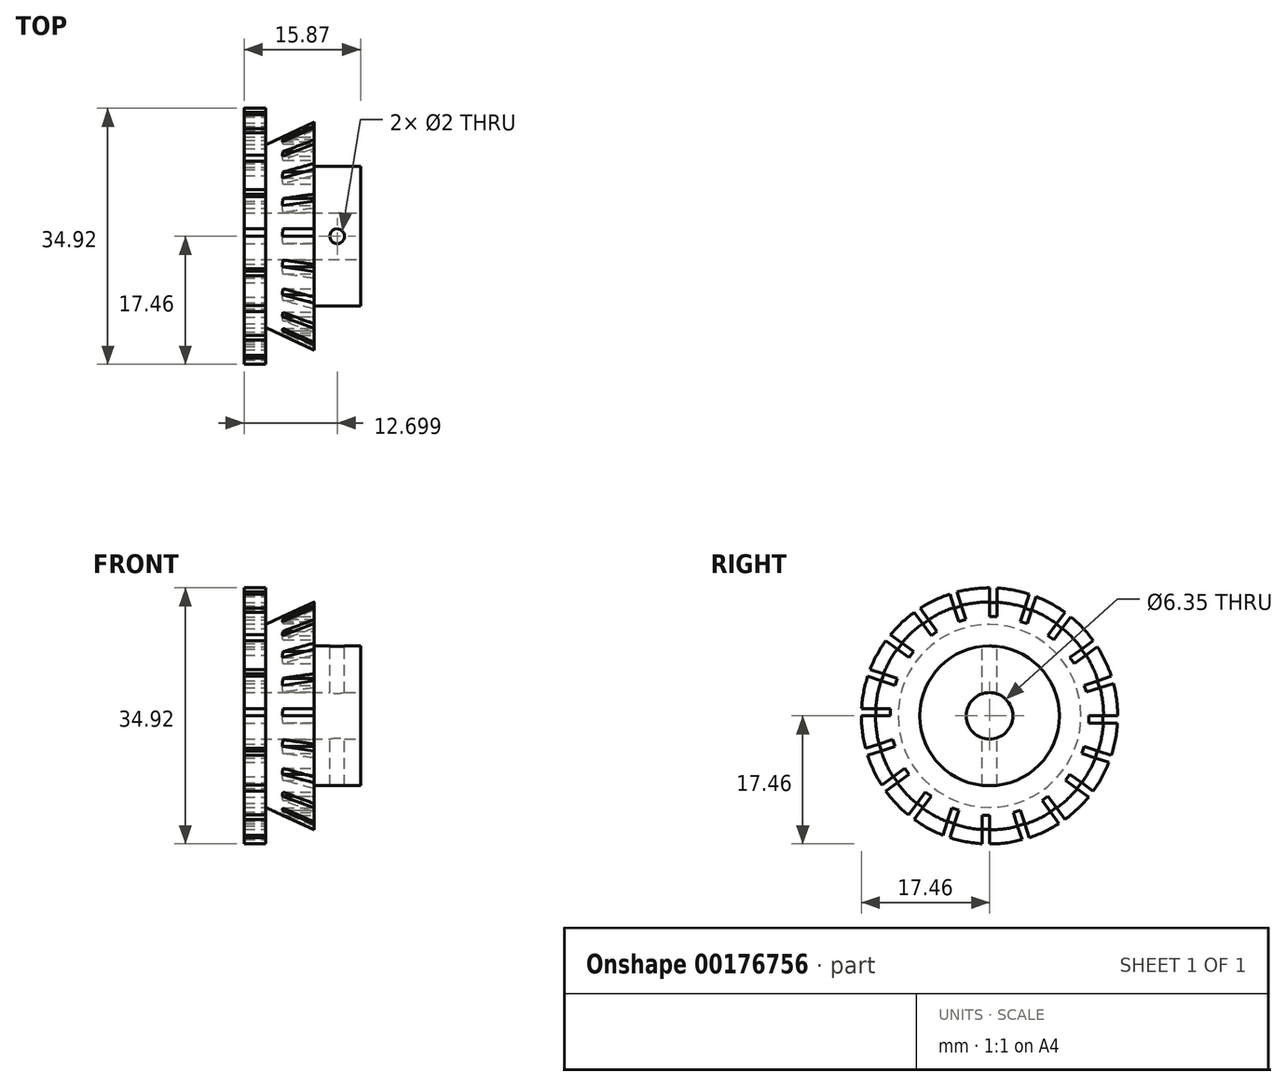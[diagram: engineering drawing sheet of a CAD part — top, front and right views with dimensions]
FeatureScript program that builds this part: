
annotation { "Feature Type Name" : "Feature", "Feature Type Description" : "" }
export const myFeature = defineFeature(function(context is Context, id is Id, definition is map)
    precondition{}
    {
        {
            var Q0;
            Q0=qCreatedBy(makeId("Front.planeOp"),FACE);
            var sketch = newSketch(context, id + "F0", { "sketchPlane" : qUnion([Q0])});
            skLineSegment(sketch, "E0", {"start": v(13.74, 3.18) * mm, "end": v(13.74, 9.53) * mm});
            skLineSegment(sketch, "E1", {"start": v(13.74, 9.53) * mm, "end": v(7.4, 9.53) * mm});
            skLineSegment(sketch, "E2", {"start": v(7.4, 9.53) * mm, "end": v(7.4, 17.46) * mm});
            skLineSegment(sketch, "E3", {"start": v(7.4, 17.46) * mm, "end": v(-2.13, 17.46) * mm});
            skLineSegment(sketch, "E4", {"start": v(-2.13, 17.46) * mm, "end": v(-2.13, 3.18) * mm});
            skLineSegment(sketch, "E5", {"start": v(-2.13, 3.18) * mm, "end": v(13.74, 3.18) * mm});
            skLineSegment(sketch, "E6", {"start": v(4.12, 0) * mm, "end": v(-4.41, 0) * mm, "construction": true});
            skSolve(sketch);
        }
        {
            var Q0;
            Q0=qSketchRegion(id+"F0",true);
            var Q1;
            Q1=sQuery(id+"F0.wireOp",EDGE,"E6");
            revolve(context, id + "F1", {"entities" : qUnion([Q0]), "axis" : qUnion([Q1]), "revolveType" : RevolveType.FULL});
        }
        {
            var Q0;
            Q0=qCreatedBy(makeId("Top.planeOp"),FACE);
            cPlane(context, id + "F2", {"entities" : qUnion([Q0]), "cplaneType" : CPlaneType.OFFSET, "offset" : 9.55 * mm, "width" : 150 * mm, "height" : 150 * mm});
        }
        {
            var Q0;
            Q0=qCreatedBy(id+"F2.planeOp",FACE);
            var sketch = newSketch(context, id + "F3", { "sketchPlane" : qUnion([Q0])});
            skCircle(sketch, "E7", {"center": v(10.57, 0) * mm, "radius": 1 * mm});
            skLineSegment(sketch, "E8.0", {"start": v(7.4, 17.46) * mm, "end": v(7.4, -17.46) * mm, "construction": true});
            skLineSegment(sketch, "E9", {"start": v(7.4, 0) * mm, "end": v(13.74, 0) * mm});
            skLineSegment(sketch, "E10.0", {"start": v(13.74, 9.53) * mm, "end": v(13.74, -9.53) * mm, "construction": true});
            skSolve(sketch);
        }
        {
            var Q0;
            Q0=qSketchRegion(id+"F3",true);
            extrude(context, id + "F4", {"entities" : qUnion([Q0]), "operationType" : NewBodyOperationType.REMOVE, "endBound" : BoundingType.THROUGH_ALL, "oppositeDirection" : true, "depth" : 25 * mm});
        }
        {
            var Q0;
            Q0=qCreatedBy(id+"F2.planeOp",FACE);
            var sketch = newSketch(context, id + "F5", { "sketchPlane" : qUnion([Q0])});
            skLineSegment(sketch, "E11", {"start": v(-2.13, 17.46) * mm, "end": v(7.4, 17.46) * mm});
            skLineSegment(sketch, "E12.0", {"start": v(-2.13, 17.46) * mm, "end": v(-2.13, -17.46) * mm});
            skLineSegment(sketch, "E13.0", {"start": v(7.4, 17.46) * mm, "end": v(7.4, -17.46) * mm});
            skSolve(sketch);
        }
        {
            var Q0;
            Q0=qCreatedBy(makeId("Top.planeOp"),FACE);
            var sketch = newSketch(context, id + "F6", { "sketchPlane" : qUnion([Q0])});
            skLineSegment(sketch, "E14.0", {"start": v(-2.13, 17.46) * mm, "end": v(-2.13, -17.46) * mm});
            skLineSegment(sketch, "E15.0", {"start": v(-2.13, 17.46) * mm, "end": v(7.4, 17.46) * mm});
            skLineSegment(sketch, "E16", {"start": v(2.63, 17.46) * mm, "end": v(2.63, 9.64) * mm, "construction": true});
            skLineSegment(sketch, "E17", {"start": v(7.4, 17.46) * mm, "end": v(-0.15, 17.46) * mm});
            skLineSegment(sketch, "E18", {"start": v(-2.13, 0) * mm, "end": v(13.75, 0) * mm, "construction": true});
            skPoint(sketch, "E18.endSnap0", {"position": v(-2.13, 0) * mm});
            skLineSegment(sketch, "E19.0", {"start": v(7.4, 17.46) * mm, "end": v(7.4, -17.46) * mm});
            skLineSegment(sketch, "E20", {"start": v(7.4, 15.54) * mm, "end": v(0.79, 12.46) * mm});
            skLineSegment(sketch, "E21", {"start": v(0.79, 12.46) * mm, "end": v(0.79, 17.46) * mm});
            skLineSegment(sketch, "E22", {"start": v(0.79, 17.46) * mm, "end": v(7.4, 17.46) * mm});
            skSolve(sketch);
        }
        {
            var Q0;
            Q0=qSketchRegion(id+"F6",true);
            var Q1;
            Q1=sQuery(id+"F6.wireOp",EDGE,"E18");
            revolve(context, id + "F7", {"operationType" : NewBodyOperationType.REMOVE, "entities" : qUnion([Q0]), "axis" : qUnion([Q1]), "revolveType" : RevolveType.FULL, "oppositeDirection" : true});
        }
        {
            var Q0;
            Q0=makeQuery(id+"F7.boolean.opBoolean","COPY",FACE,{"derivedFrom":makeQuery(id+"F7.opRevolve","SWEPT_FACE",FACE,{"disambiguationData":[OSD([sQuery(id+"F6.wireOp",EDGE,"E21")])]})});
            var sketch = newSketch(context, id + "F8", { "sketchPlane" : qUnion([Q0])});
            skLineSegment(sketch, "E23", {"start": v(0, 18.46) * mm, "end": v(0, 15.46) * mm});
            skLineSegment(sketch, "E24", {"start": v(0, 15.46) * mm, "end": v(1, 15.46) * mm});
            skLineSegment(sketch, "E25", {"start": v(1, 15.46) * mm, "end": v(1, 18.46) * mm});
            skLineSegment(sketch, "E26", {"start": v(1, 18.46) * mm, "end": v(0, 18.46) * mm});
            skLineSegment(sketch, "E27.1.0", {"start": v(-4.75, 17.87) * mm, "end": v(-5.7, 17.56) * mm});
            skLineSegment(sketch, "E27.1.1", {"start": v(-3.83, 15.01) * mm, "end": v(-4.75, 17.87) * mm});
            skLineSegment(sketch, "E27.1.2", {"start": v(-5.7, 17.56) * mm, "end": v(-4.78, 14.7) * mm});
            skLineSegment(sketch, "E27.1.3", {"start": v(-4.78, 14.7) * mm, "end": v(-3.83, 15.01) * mm});
            skLineSegment(sketch, "E27.2.0", {"start": v(-10.04, 15.52) * mm, "end": v(-10.85, 14.94) * mm});
            skLineSegment(sketch, "E27.2.1", {"start": v(-8.28, 13.1) * mm, "end": v(-10.04, 15.52) * mm});
            skLineSegment(sketch, "E27.2.2", {"start": v(-10.85, 14.94) * mm, "end": v(-9.09, 12.5) * mm});
            skLineSegment(sketch, "E27.2.3", {"start": v(-9.09, 12.5) * mm, "end": v(-8.28, 13.1) * mm});
            skLineSegment(sketch, "E27.3.0", {"start": v(-14.35, 11.66) * mm, "end": v(-14.94, 10.85) * mm});
            skLineSegment(sketch, "E27.3.1", {"start": v(-11.92, 9.9) * mm, "end": v(-14.35, 11.66) * mm});
            skLineSegment(sketch, "E27.3.2", {"start": v(-14.94, 10.85) * mm, "end": v(-12.5, 9.09) * mm});
            skLineSegment(sketch, "E27.3.3", {"start": v(-12.5, 9.09) * mm, "end": v(-11.92, 9.9) * mm});
            skLineSegment(sketch, "E27.4.0", {"start": v(-17.25, 6.66) * mm, "end": v(-17.56, 5.7) * mm});
            skLineSegment(sketch, "E27.4.1", {"start": v(-14.4, 5.73) * mm, "end": v(-17.25, 6.66) * mm});
            skLineSegment(sketch, "E27.4.2", {"start": v(-17.56, 5.7) * mm, "end": v(-14.7, 4.78) * mm});
            skLineSegment(sketch, "E27.4.3", {"start": v(-14.7, 4.78) * mm, "end": v(-14.4, 5.73) * mm});
            skLineSegment(sketch, "E27.5.0", {"start": v(-18.46, 1) * mm, "end": v(-18.46, 0) * mm});
            skLineSegment(sketch, "E27.5.1", {"start": v(-15.46, 1) * mm, "end": v(-18.46, 1) * mm});
            skLineSegment(sketch, "E27.5.2", {"start": v(-18.46, 0) * mm, "end": v(-15.46, 0) * mm});
            skLineSegment(sketch, "E27.5.3", {"start": v(-15.46, 0) * mm, "end": v(-15.46, 1) * mm});
            skLineSegment(sketch, "E27.6.0", {"start": v(-17.87, -4.75) * mm, "end": v(-17.56, -5.7) * mm});
            skLineSegment(sketch, "E27.6.1", {"start": v(-15.01, -3.83) * mm, "end": v(-17.87, -4.75) * mm});
            skLineSegment(sketch, "E27.6.2", {"start": v(-17.56, -5.7) * mm, "end": v(-14.7, -4.78) * mm});
            skLineSegment(sketch, "E27.6.3", {"start": v(-14.7, -4.78) * mm, "end": v(-15.01, -3.83) * mm});
            skLineSegment(sketch, "E27.7.0", {"start": v(-15.52, -10.04) * mm, "end": v(-14.94, -10.85) * mm});
            skLineSegment(sketch, "E27.7.1", {"start": v(-13.1, -8.28) * mm, "end": v(-15.52, -10.04) * mm});
            skLineSegment(sketch, "E27.7.2", {"start": v(-14.94, -10.85) * mm, "end": v(-12.5, -9.09) * mm});
            skLineSegment(sketch, "E27.7.3", {"start": v(-12.5, -9.09) * mm, "end": v(-13.1, -8.28) * mm});
            skLineSegment(sketch, "E27.8.0", {"start": v(-11.66, -14.35) * mm, "end": v(-10.85, -14.94) * mm});
            skLineSegment(sketch, "E27.8.1", {"start": v(-9.9, -11.92) * mm, "end": v(-11.66, -14.35) * mm});
            skLineSegment(sketch, "E27.8.2", {"start": v(-10.85, -14.94) * mm, "end": v(-9.09, -12.5) * mm});
            skLineSegment(sketch, "E27.8.3", {"start": v(-9.09, -12.5) * mm, "end": v(-9.9, -11.92) * mm});
            skLineSegment(sketch, "E27.9.0", {"start": v(-6.66, -17.25) * mm, "end": v(-5.7, -17.56) * mm});
            skLineSegment(sketch, "E27.9.1", {"start": v(-5.73, -14.4) * mm, "end": v(-6.66, -17.25) * mm});
            skLineSegment(sketch, "E27.9.2", {"start": v(-5.7, -17.56) * mm, "end": v(-4.78, -14.7) * mm});
            skLineSegment(sketch, "E27.9.3", {"start": v(-4.78, -14.7) * mm, "end": v(-5.73, -14.4) * mm});
            skLineSegment(sketch, "E27.10.0", {"start": v(-1, -18.46) * mm, "end": v(0, -18.46) * mm});
            skLineSegment(sketch, "E27.10.1", {"start": v(-1, -15.46) * mm, "end": v(-1, -18.46) * mm});
            skLineSegment(sketch, "E27.10.2", {"start": v(0, -18.46) * mm, "end": v(0, -15.46) * mm});
            skLineSegment(sketch, "E27.10.3", {"start": v(0, -15.46) * mm, "end": v(-1, -15.46) * mm});
            skLineSegment(sketch, "E27.11.0", {"start": v(4.75, -17.87) * mm, "end": v(5.7, -17.56) * mm});
            skLineSegment(sketch, "E27.11.1", {"start": v(3.83, -15.01) * mm, "end": v(4.75, -17.87) * mm});
            skLineSegment(sketch, "E27.11.2", {"start": v(5.7, -17.56) * mm, "end": v(4.78, -14.7) * mm});
            skLineSegment(sketch, "E27.11.3", {"start": v(4.78, -14.7) * mm, "end": v(3.83, -15.01) * mm});
            skLineSegment(sketch, "E27.12.0", {"start": v(10.04, -15.52) * mm, "end": v(10.85, -14.94) * mm});
            skLineSegment(sketch, "E27.12.1", {"start": v(8.28, -13.1) * mm, "end": v(10.04, -15.52) * mm});
            skLineSegment(sketch, "E27.12.2", {"start": v(10.85, -14.94) * mm, "end": v(9.09, -12.5) * mm});
            skLineSegment(sketch, "E27.12.3", {"start": v(9.09, -12.5) * mm, "end": v(8.28, -13.1) * mm});
            skLineSegment(sketch, "E27.13.0", {"start": v(14.35, -11.66) * mm, "end": v(14.94, -10.85) * mm});
            skLineSegment(sketch, "E27.13.1", {"start": v(11.92, -9.9) * mm, "end": v(14.35, -11.66) * mm});
            skLineSegment(sketch, "E27.13.2", {"start": v(14.94, -10.85) * mm, "end": v(12.5, -9.09) * mm});
            skLineSegment(sketch, "E27.13.3", {"start": v(12.5, -9.09) * mm, "end": v(11.92, -9.9) * mm});
            skLineSegment(sketch, "E27.14.0", {"start": v(17.25, -6.66) * mm, "end": v(17.56, -5.7) * mm});
            skLineSegment(sketch, "E27.14.1", {"start": v(14.4, -5.73) * mm, "end": v(17.25, -6.66) * mm});
            skLineSegment(sketch, "E27.14.2", {"start": v(17.56, -5.7) * mm, "end": v(14.7, -4.78) * mm});
            skLineSegment(sketch, "E27.14.3", {"start": v(14.7, -4.78) * mm, "end": v(14.4, -5.73) * mm});
            skLineSegment(sketch, "E27.15.0", {"start": v(18.46, -1) * mm, "end": v(18.46, 0) * mm});
            skLineSegment(sketch, "E27.15.1", {"start": v(15.46, -1) * mm, "end": v(18.46, -1) * mm});
            skLineSegment(sketch, "E27.15.2", {"start": v(18.46, 0) * mm, "end": v(15.46, 0) * mm});
            skLineSegment(sketch, "E27.15.3", {"start": v(15.46, 0) * mm, "end": v(15.46, -1) * mm});
            skLineSegment(sketch, "E27.16.0", {"start": v(17.87, 4.75) * mm, "end": v(17.56, 5.7) * mm});
            skLineSegment(sketch, "E27.16.1", {"start": v(15.01, 3.83) * mm, "end": v(17.87, 4.75) * mm});
            skLineSegment(sketch, "E27.16.2", {"start": v(17.56, 5.7) * mm, "end": v(14.7, 4.78) * mm});
            skLineSegment(sketch, "E27.16.3", {"start": v(14.7, 4.78) * mm, "end": v(15.01, 3.83) * mm});
            skLineSegment(sketch, "E27.17.0", {"start": v(15.52, 10.04) * mm, "end": v(14.94, 10.85) * mm});
            skLineSegment(sketch, "E27.17.1", {"start": v(13.1, 8.28) * mm, "end": v(15.52, 10.04) * mm});
            skLineSegment(sketch, "E27.17.2", {"start": v(14.94, 10.85) * mm, "end": v(12.5, 9.09) * mm});
            skLineSegment(sketch, "E27.17.3", {"start": v(12.5, 9.09) * mm, "end": v(13.1, 8.28) * mm});
            skLineSegment(sketch, "E27.18.0", {"start": v(11.66, 14.35) * mm, "end": v(10.85, 14.94) * mm});
            skLineSegment(sketch, "E27.18.1", {"start": v(9.9, 11.92) * mm, "end": v(11.66, 14.35) * mm});
            skLineSegment(sketch, "E27.18.2", {"start": v(10.85, 14.94) * mm, "end": v(9.09, 12.5) * mm});
            skLineSegment(sketch, "E27.18.3", {"start": v(9.09, 12.5) * mm, "end": v(9.9, 11.92) * mm});
            skLineSegment(sketch, "E27.19.0", {"start": v(6.66, 17.25) * mm, "end": v(5.7, 17.56) * mm});
            skLineSegment(sketch, "E27.19.1", {"start": v(5.73, 14.4) * mm, "end": v(6.66, 17.25) * mm});
            skLineSegment(sketch, "E27.19.2", {"start": v(5.7, 17.56) * mm, "end": v(4.78, 14.7) * mm});
            skLineSegment(sketch, "E27.19.3", {"start": v(4.78, 14.7) * mm, "end": v(5.73, 14.4) * mm});
            skPoint(sketch, "E27.center", {"position": v(0, 0) * mm});
            skSolve(sketch);
        }
        {
            var Q0;
            Q0 = qSketchRegion(id + "F8", true);
            extrude(context, id + "F9", {"entities" : qUnion([Q0]), "operationType" : NewBodyOperationType.REMOVE, "endBound" : BoundingType.THROUGH_ALL, "oppositeDirection" : true, "depth" : 25 * mm});
        }
        {
            var Q0;
            Q0=makeQuery(id+"F1.opRevolve","SWEPT_FACE",FACE,{"disambiguationData":[OSD([sQuery(id+"F0.wireOp",EDGE,"E2")])]});
            var sketch = newSketch(context, id + "F10", { "sketchPlane" : qUnion([Q0])});
            skLineSegment(sketch, "E28", {"start": v(0, 16.41) * mm, "end": v(0, 13.54) * mm});
            skLineSegment(sketch, "E29", {"start": v(0, 13.54) * mm, "end": v(1, 13.54) * mm});
            skLineSegment(sketch, "E30", {"start": v(1, 13.54) * mm, "end": v(1, 16.41) * mm});
            skLineSegment(sketch, "E31", {"start": v(1, 16.41) * mm, "end": v(0, 16.41) * mm});
            skLineSegment(sketch, "E32.1.0", {"start": v(-3.23, 13.19) * mm, "end": v(-4.12, 15.92) * mm});
            skLineSegment(sketch, "E32.1.1", {"start": v(-5.07, 15.6) * mm, "end": v(-4.18, 12.88) * mm});
            skLineSegment(sketch, "E32.1.2", {"start": v(-4.12, 15.92) * mm, "end": v(-5.07, 15.6) * mm});
            skLineSegment(sketch, "E32.1.3", {"start": v(-4.18, 12.88) * mm, "end": v(-3.23, 13.19) * mm});
            skLineSegment(sketch, "E32.2.0", {"start": v(-7.15, 11.54) * mm, "end": v(-8.84, 13.86) * mm});
            skLineSegment(sketch, "E32.2.1", {"start": v(-9.65, 13.28) * mm, "end": v(-7.96, 10.96) * mm});
            skLineSegment(sketch, "E32.2.2", {"start": v(-8.84, 13.86) * mm, "end": v(-9.65, 13.28) * mm});
            skLineSegment(sketch, "E32.2.3", {"start": v(-7.96, 10.96) * mm, "end": v(-7.15, 11.54) * mm});
            skLineSegment(sketch, "E32.3.0", {"start": v(-10.37, 8.77) * mm, "end": v(-12.69, 10.45) * mm});
            skLineSegment(sketch, "E32.3.1", {"start": v(-13.28, 9.65) * mm, "end": v(-10.96, 7.96) * mm});
            skLineSegment(sketch, "E32.3.2", {"start": v(-12.69, 10.45) * mm, "end": v(-13.28, 9.65) * mm});
            skLineSegment(sketch, "E32.3.3", {"start": v(-10.96, 7.96) * mm, "end": v(-10.37, 8.77) * mm});
            skLineSegment(sketch, "E32.4.0", {"start": v(-12.57, 5.14) * mm, "end": v(-15.3, 6.02) * mm});
            skLineSegment(sketch, "E32.4.1", {"start": v(-15.6, 5.07) * mm, "end": v(-12.88, 4.18) * mm});
            skLineSegment(sketch, "E32.4.2", {"start": v(-15.3, 6.02) * mm, "end": v(-15.6, 5.07) * mm});
            skLineSegment(sketch, "E32.4.3", {"start": v(-12.88, 4.18) * mm, "end": v(-12.57, 5.14) * mm});
            skLineSegment(sketch, "E32.5.0", {"start": v(-13.54, 1) * mm, "end": v(-16.41, 1) * mm});
            skLineSegment(sketch, "E32.5.1", {"start": v(-16.41, 0) * mm, "end": v(-13.54, 0) * mm});
            skLineSegment(sketch, "E32.5.2", {"start": v(-16.41, 1) * mm, "end": v(-16.41, 0) * mm});
            skLineSegment(sketch, "E32.5.3", {"start": v(-13.54, 0) * mm, "end": v(-13.54, 1) * mm});
            skLineSegment(sketch, "E32.6.0", {"start": v(-13.19, -3.23) * mm, "end": v(-15.92, -4.12) * mm});
            skLineSegment(sketch, "E32.6.1", {"start": v(-15.6, -5.07) * mm, "end": v(-12.88, -4.18) * mm});
            skLineSegment(sketch, "E32.6.2", {"start": v(-15.92, -4.12) * mm, "end": v(-15.6, -5.07) * mm});
            skLineSegment(sketch, "E32.6.3", {"start": v(-12.88, -4.18) * mm, "end": v(-13.19, -3.23) * mm});
            skLineSegment(sketch, "E32.7.0", {"start": v(-11.54, -7.15) * mm, "end": v(-13.86, -8.84) * mm});
            skLineSegment(sketch, "E32.7.1", {"start": v(-13.28, -9.65) * mm, "end": v(-10.96, -7.96) * mm});
            skLineSegment(sketch, "E32.7.2", {"start": v(-13.86, -8.84) * mm, "end": v(-13.28, -9.65) * mm});
            skLineSegment(sketch, "E32.7.3", {"start": v(-10.96, -7.96) * mm, "end": v(-11.54, -7.15) * mm});
            skLineSegment(sketch, "E32.8.0", {"start": v(-8.77, -10.37) * mm, "end": v(-10.45, -12.69) * mm});
            skLineSegment(sketch, "E32.8.1", {"start": v(-9.65, -13.28) * mm, "end": v(-7.96, -10.96) * mm});
            skLineSegment(sketch, "E32.8.2", {"start": v(-10.45, -12.69) * mm, "end": v(-9.65, -13.28) * mm});
            skLineSegment(sketch, "E32.8.3", {"start": v(-7.96, -10.96) * mm, "end": v(-8.77, -10.37) * mm});
            skLineSegment(sketch, "E32.9.0", {"start": v(-5.14, -12.57) * mm, "end": v(-6.02, -15.3) * mm});
            skLineSegment(sketch, "E32.9.1", {"start": v(-5.07, -15.6) * mm, "end": v(-4.18, -12.88) * mm});
            skLineSegment(sketch, "E32.9.2", {"start": v(-6.02, -15.3) * mm, "end": v(-5.07, -15.6) * mm});
            skLineSegment(sketch, "E32.9.3", {"start": v(-4.18, -12.88) * mm, "end": v(-5.14, -12.57) * mm});
            skLineSegment(sketch, "E32.10.0", {"start": v(-1, -13.54) * mm, "end": v(-1, -16.41) * mm});
            skLineSegment(sketch, "E32.10.1", {"start": v(0, -16.41) * mm, "end": v(0, -13.54) * mm});
            skLineSegment(sketch, "E32.10.2", {"start": v(-1, -16.41) * mm, "end": v(0, -16.41) * mm});
            skLineSegment(sketch, "E32.10.3", {"start": v(0, -13.54) * mm, "end": v(-1, -13.54) * mm});
            skLineSegment(sketch, "E32.11.0", {"start": v(3.23, -13.19) * mm, "end": v(4.12, -15.92) * mm});
            skLineSegment(sketch, "E32.11.1", {"start": v(5.07, -15.6) * mm, "end": v(4.18, -12.88) * mm});
            skLineSegment(sketch, "E32.11.2", {"start": v(4.12, -15.92) * mm, "end": v(5.07, -15.6) * mm});
            skLineSegment(sketch, "E32.11.3", {"start": v(4.18, -12.88) * mm, "end": v(3.23, -13.19) * mm});
            skLineSegment(sketch, "E32.12.0", {"start": v(7.15, -11.54) * mm, "end": v(8.84, -13.86) * mm});
            skLineSegment(sketch, "E32.12.1", {"start": v(9.65, -13.28) * mm, "end": v(7.96, -10.96) * mm});
            skLineSegment(sketch, "E32.12.2", {"start": v(8.84, -13.86) * mm, "end": v(9.65, -13.28) * mm});
            skLineSegment(sketch, "E32.12.3", {"start": v(7.96, -10.96) * mm, "end": v(7.15, -11.54) * mm});
            skLineSegment(sketch, "E32.13.0", {"start": v(10.37, -8.77) * mm, "end": v(12.69, -10.45) * mm});
            skLineSegment(sketch, "E32.13.1", {"start": v(13.28, -9.65) * mm, "end": v(10.96, -7.96) * mm});
            skLineSegment(sketch, "E32.13.2", {"start": v(12.69, -10.45) * mm, "end": v(13.28, -9.65) * mm});
            skLineSegment(sketch, "E32.13.3", {"start": v(10.96, -7.96) * mm, "end": v(10.37, -8.77) * mm});
            skLineSegment(sketch, "E32.14.0", {"start": v(12.57, -5.14) * mm, "end": v(15.3, -6.02) * mm});
            skLineSegment(sketch, "E32.14.1", {"start": v(15.6, -5.07) * mm, "end": v(12.88, -4.18) * mm});
            skLineSegment(sketch, "E32.14.2", {"start": v(15.3, -6.02) * mm, "end": v(15.6, -5.07) * mm});
            skLineSegment(sketch, "E32.14.3", {"start": v(12.88, -4.18) * mm, "end": v(12.57, -5.14) * mm});
            skLineSegment(sketch, "E32.15.0", {"start": v(13.54, -1) * mm, "end": v(16.41, -1) * mm});
            skLineSegment(sketch, "E32.15.1", {"start": v(16.41, 0) * mm, "end": v(13.54, 0) * mm});
            skLineSegment(sketch, "E32.15.2", {"start": v(16.41, -1) * mm, "end": v(16.41, 0) * mm});
            skLineSegment(sketch, "E32.15.3", {"start": v(13.54, 0) * mm, "end": v(13.54, -1) * mm});
            skLineSegment(sketch, "E32.16.0", {"start": v(13.19, 3.23) * mm, "end": v(15.92, 4.12) * mm});
            skLineSegment(sketch, "E32.16.1", {"start": v(15.6, 5.07) * mm, "end": v(12.88, 4.18) * mm});
            skLineSegment(sketch, "E32.16.2", {"start": v(15.92, 4.12) * mm, "end": v(15.6, 5.07) * mm});
            skLineSegment(sketch, "E32.16.3", {"start": v(12.88, 4.18) * mm, "end": v(13.19, 3.23) * mm});
            skLineSegment(sketch, "E32.17.0", {"start": v(11.54, 7.15) * mm, "end": v(13.86, 8.84) * mm});
            skLineSegment(sketch, "E32.17.1", {"start": v(13.28, 9.65) * mm, "end": v(10.96, 7.96) * mm});
            skLineSegment(sketch, "E32.17.2", {"start": v(13.86, 8.84) * mm, "end": v(13.28, 9.65) * mm});
            skLineSegment(sketch, "E32.17.3", {"start": v(10.96, 7.96) * mm, "end": v(11.54, 7.15) * mm});
            skLineSegment(sketch, "E32.18.0", {"start": v(8.77, 10.37) * mm, "end": v(10.45, 12.69) * mm});
            skLineSegment(sketch, "E32.18.1", {"start": v(9.65, 13.28) * mm, "end": v(7.96, 10.96) * mm});
            skLineSegment(sketch, "E32.18.2", {"start": v(10.45, 12.69) * mm, "end": v(9.65, 13.28) * mm});
            skLineSegment(sketch, "E32.18.3", {"start": v(7.96, 10.96) * mm, "end": v(8.77, 10.37) * mm});
            skLineSegment(sketch, "E32.19.0", {"start": v(5.14, 12.57) * mm, "end": v(6.02, 15.3) * mm});
            skLineSegment(sketch, "E32.19.1", {"start": v(5.07, 15.6) * mm, "end": v(4.18, 12.88) * mm});
            skLineSegment(sketch, "E32.19.2", {"start": v(6.02, 15.3) * mm, "end": v(5.07, 15.6) * mm});
            skLineSegment(sketch, "E32.19.3", {"start": v(4.18, 12.88) * mm, "end": v(5.14, 12.57) * mm});
            skPoint(sketch, "E32.center", {"position": v(0, 0) * mm});
            skSolve(sketch);
        }
        {
            var Q0;
            Q0 = qSketchRegion(id + "F10", true);
            extrude(context, id + "F11", {"entities" : qUnion([Q0]), "operationType" : NewBodyOperationType.REMOVE, "oppositeDirection" : true, "depth" : 5 * mm});
        }
    });
